# Revit family: Indoor_Wall Lamp_Santa&Cole_Estadio Aplique Singular
name_source: partatom
category: Luminarias
units: mm (PartAtom-declared; Revit-internal decimal feet)

## family parameters
Compartido = No
Corte con vacíos al cargar = No
Cota de conector redondo = Diámetro de uso
Número OmniClass = 23.80.70.00
Origen de luz = Sí
Punto de cálculo de habitación = No
Se basa en plano de trabajo = Sí
Siempre vertical = Sí
Tipo de pieza = Normal
Título OmniClass = Lighting

## types (2) — shared parameters
Archivo de red fotométrica = ESTWB01 (CL004A22F004G).IES
Assembly instructions - CE = https://www.santacole.com
Assembly instructions - UL = https://www.santacole.com
Cambio de temperatura de color de luz atenuada = <Ninguno>
Carga aparente = 6 VA
Code = ESTWB01
Elevación por defecto = 1219 mm
Fabricante = Santa & Cole
Filtro de color = 16777215
Manufacturer website = https://www.santacole.com
Material = <Por categoría>
Modelo = Estadio Singular
Technical Information = https://www.santacole.com
URL = https://www.santacole.com
Voltaje (90-305 V) = 220 V
Ángulo de inclinación = 90.00°

## per-type parameters (varying)
| type | Material Estructura |
| Estadio Aplique Singular - Negro | Santa & Cole - Black Anodized Aluminium |
| Estadio Aplique Singular - Blanco | Santa & Cole - White Matte Metal |

## geometry (parser evidence)
native form markers: Sweep x3
no freeform markers — native parametric forms only
